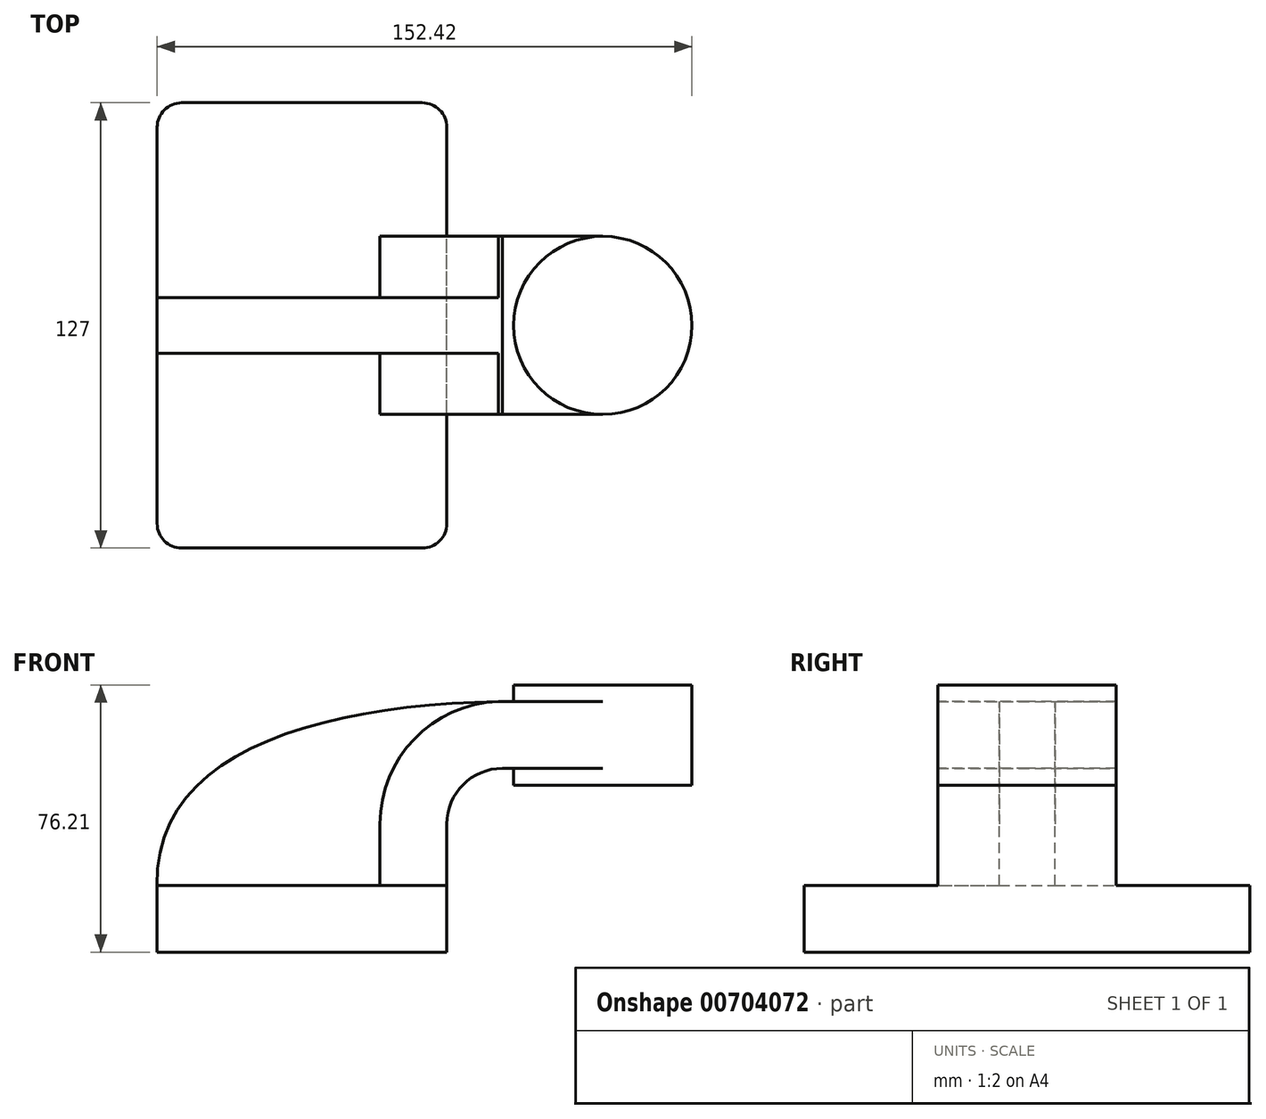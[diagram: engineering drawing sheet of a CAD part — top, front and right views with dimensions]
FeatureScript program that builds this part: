
annotation { "Feature Type Name" : "Feature", "Feature Type Description" : "" }
export const myFeature = defineFeature(function(context is Context, id is Id, definition is map)
    precondition{}
    {
        {
            var Q0;
            Q0=qCreatedBy(makeId("Front.planeOp"),FACE);
            var sketch = newSketch(context, id + "F0", { "sketchPlane" : qUnion([Q0])});
            skLineSegment(sketch, "E0.bottom", {"start": v(41.27, 9.53) * mm, "end": v(-41.28, 9.53) * mm});
            skLineSegment(sketch, "E0.top", {"start": v(41.28, -9.52) * mm, "end": v(-41.27, -9.52) * mm});
            skLineSegment(sketch, "E0.left", {"start": v(41.28, 9.53) * mm, "end": v(41.28, -9.52) * mm});
            skLineSegment(sketch, "E0.right", {"start": v(-41.28, 9.53) * mm, "end": v(-41.27, -9.52) * mm});
            skPoint(sketch, "E0.middle", {"position": v(0, 0) * mm});
            skLineSegment(sketch, "E1.bottom", {"start": v(111.12, 66.68) * mm, "end": v(60.32, 66.68) * mm});
            skLineSegment(sketch, "E1.top", {"start": v(111.12, 38.1) * mm, "end": v(60.32, 38.1) * mm});
            skLineSegment(sketch, "E1.left", {"start": v(111.13, 66.68) * mm, "end": v(111.13, 38.1) * mm});
            skLineSegment(sketch, "E1.right", {"start": v(60.32, 66.68) * mm, "end": v(60.32, 38.1) * mm});
            skPoint(sketch, "E1.middle", {"position": v(85.72, 52.39) * mm});
            skLineSegment(sketch, "E2", {"start": v(41.27, 9.53) * mm, "end": v(41.27, 27) * mm});
            skArc(sketch, "E3", {"start": v(41.27, 27) * mm, "mid": v(45.92, 38.23) * mm, "end": v(57.15, 42.88) * mm});
            skLineSegment(sketch, "E4", {"start": v(57.15, 42.88) * mm, "end": v(85.72, 42.88) * mm});
            skLineSegment(sketch, "E5.0", {"start": v(57.15, 61.93) * mm, "end": v(85.72, 61.93) * mm});
            skArc(sketch, "E5.1", {"start": v(22.23, 27) * mm, "mid": v(32.45, 51.7) * mm, "end": v(57.15, 61.93) * mm});
            skLineSegment(sketch, "E5.2", {"start": v(22.22, 9.53) * mm, "end": v(22.22, 27) * mm});
            skLineSegment(sketch, "E6", {"start": v(85.72, 38.1) * mm, "end": v(85.72, 66.68) * mm});
            skFitSpline(sketch, "E7", {"points": [v(-41.28, 9.52) * mm, v(57.15, 61.93) * mm], "startDerivative": vector(-2.93, 115.08) * mm, "endDerivative": vector(155.05, 2.35) * mm});
            skSolve(sketch);
        }
        {
            var Q0;
            Q0=makeQuery(id+"F0.imprint","IMPRINT",FACE,{"disambiguationData":[TD([[makeQuery(id+"F0.imprint","IMPRINT",EDGE,{"derivedFrom":sQuery(id+"F0.wireOp",EDGE,"E0.top")}),-1.0]])]});
            extrude(context, id + "F1", {"entities" : qUnion([Q0]), "endBound" : BoundingType.SYMMETRIC, "depth" : 127 * mm, "offsetDistance" : 25.4 * mm});
        }
        {
            var Q0;
            {var subQ1=sQuery(id+"F0.wireOp",EDGE,"E2");Q0=makeQuery(id+"F0.imprint","IMPRINT",FACE,{"disambiguationData":[TD([[makeQuery(id+"F0.imprint","IMPRINT",EDGE,{"derivedFrom":subQ1}),1.0]])]});}
            var Q1;
            {var subQ0=sQuery(id+"F0.wireOp",EDGE,"E5.0");var subQ1=sQuery(id+"F0.wireOp",EDGE,"E1.right");var subQ2=makeQuery(id+"F0.imprint","INTERSECT",VERTEX,{"derivedFrom":[subQ1,subQ0]});Q1=makeQuery(id+"F0.imprint","IMPRINT",FACE,{"disambiguationData":[TD([[makeQuery(id+"F0.imprint","IMPRINT",EDGE,{"disambiguationData":[TD([[subQ2,-1.0]])],"derivedFrom":subQ1}),1.0]])]});}
            extrude(context, id + "F2", {"entities" : qUnion([Q0, Q1]), "operationType" : NewBodyOperationType.ADD, "endBound" : BoundingType.SYMMETRIC, "depth" : 50.8 * mm, "offsetDistance" : 25.4 * mm});
        }
        {
            var Q0;
            {var subQ3=sQuery(id+"F0.wireOp",EDGE,"E5.2");Q0=makeQuery(id+"F0.imprint","IMPRINT",FACE,{"disambiguationData":[TD([[makeQuery(id+"F0.imprint","IMPRINT",EDGE,{"derivedFrom":subQ3}),1.0]])]});}
            extrude(context, id + "F3", {"entities" : qUnion([Q0]), "operationType" : NewBodyOperationType.ADD, "endBound" : BoundingType.SYMMETRIC, "depth" : 15.88 * mm, "offsetDistance" : 25.4 * mm});
        }
        {
            var Q0;
            {var subQ0=sQuery(id+"F0.wireOp",EDGE,"E1.left");Q0=makeQuery(id+"F0.imprint","IMPRINT",FACE,{"disambiguationData":[TD([[makeQuery(id+"F0.imprint","IMPRINT",EDGE,{"derivedFrom":subQ0}),-1.0]])]});}
            var Q1;
            Q1=sQuery(id+"F0.wireOp",EDGE,"E6");
            revolve(context, id + "F4", {"operationType" : NewBodyOperationType.ADD, "entities" : qUnion([Q0]), "axis" : qUnion([Q1]), "revolveType" : RevolveType.FULL});
        }
        {
            var Q0;
            Q0=makeQuery(id+"F1.opExtrude","CAP_EDGE",EDGE,{"disambiguationData":[OSD([sQuery(id+"F0.wireOp",EDGE,"E0.right")])],"isStart":false});
            var Q1;
            Q1=makeQuery(id+"F1.opExtrude","CAP_EDGE",EDGE,{"disambiguationData":[OSD([sQuery(id+"F0.wireOp",EDGE,"E0.left")])],"isStart":false});
            var Q2;
            Q2=makeQuery(id+"F1.opExtrude","CAP_EDGE",EDGE,{"disambiguationData":[OSD([sQuery(id+"F0.wireOp",EDGE,"E0.left")])],"isStart":true});
            var Q3;
            Q3=makeQuery(id+"F1.opExtrude","CAP_EDGE",EDGE,{"disambiguationData":[OSD([sQuery(id+"F0.wireOp",EDGE,"E0.right")])],"isStart":true});
            fillet(context, id + "F5", {"entities" : qUnion([Q0, Q1, Q2, Q3]), "radius" : 7 * mm, "tangentPropagation" : true, "allowEdgeOverflow" : false});
        }
    });
